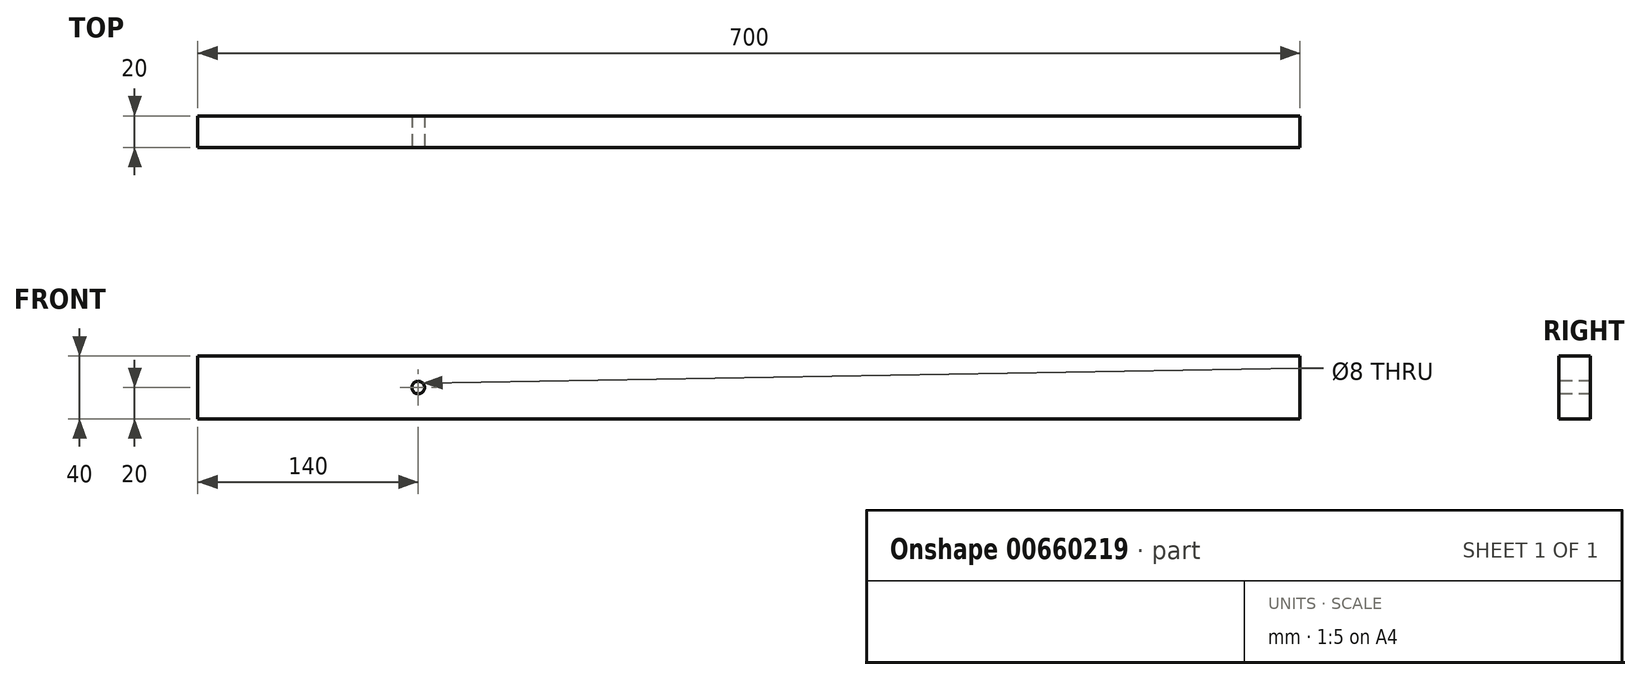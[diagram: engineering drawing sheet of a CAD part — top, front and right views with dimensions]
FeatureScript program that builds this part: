
annotation { "Feature Type Name" : "Feature", "Feature Type Description" : "" }
export const myFeature = defineFeature(function(context is Context, id is Id, definition is map)
    precondition{}
    {
        {
            var Q0;
            Q0=qCreatedBy(makeId("Top.planeOp"),FACE);
            var sketch = newSketch(context, id + "F0", { "sketchPlane" : qUnion([Q0])});
            skLineSegment(sketch, "E0", {"start": v(0, 0) * mm, "end": v(700, 0) * mm, "construction": true});
            skLineSegment(sketch, "E1", {"start": v(700, 10) * mm, "end": v(700, -10) * mm});
            skLineSegment(sketch, "E2", {"start": v(700, 10) * mm, "end": v(0.36, 10) * mm});
            skLineSegment(sketch, "E3", {"start": v(700, -10) * mm, "end": v(0, -10) * mm});
            skLineSegment(sketch, "E4", {"start": v(0, -10) * mm, "end": v(0, 10) * mm});
            skLineSegment(sketch, "E5", {"start": v(0.36, 10) * mm, "end": v(0, 10) * mm});
            skPoint(sketch, "E6.orphan", {"position": v(0, -11.32) * mm});
            skSolve(sketch);
        }
        {
            var Q0;
            Q0 = qSketchRegion(id + "F0", true);
            extrude(context, id + "F1", {"entities" : qUnion([Q0]), "depth" : 40 * mm, "offsetDistance" : 25 * mm});
        }
        {
            var Q0;
            Q0=makeQuery(id+"F1.opExtrude","SWEPT_FACE",FACE,{"disambiguationData":[OSD([sQuery(id+"F0.wireOp",EDGE,"E3")])]});
            var sketch = newSketch(context, id + "F2", { "sketchPlane" : qUnion([Q0])});
            skCircle(sketch, "E7", {"center": v(140, 20) * mm, "radius": 4 * mm});
            skSolve(sketch);
        }
        {
            var Q0;
            Q0 = qSketchRegion(id + "F2", true);
            extrude(context, id + "F3", {"entities" : qUnion([Q0]), "operationType" : NewBodyOperationType.REMOVE, "oppositeDirection" : true, "depth" : 25 * mm, "offsetDistance" : 25 * mm});
        }
    });
